# Revit family: Grohe_PlumbingFixtures_GrohthermSquare_ThermostaticMixer_24078000a
name_source: partatom
category: Plumbing Fixtures
revit_build: Autodesk Revit 2016 (Build: 20150714_1515(x64)
units: mm (PartAtom-declared; Revit-internal decimal feet)

## family parameters
Cut with Voids When Loaded = No
Host = Face
OmniClass Number = 23.65.00.00
OmniClass Title = Supply and Distribution of Liquids and Gases
Part Type = Normal
Room Calculation Point = No
Round Connector Dimension = Use Diameter
Shared = No

## types (1)
- 24078000
    ADACompliant = No
    Assembly Code = C1030
    AssetType = Fixed
    BIMObjectName = Grohe_PlumbingFixtures_GrohthermSquare_ThermostaticMixer_24078000
    CWFU = 4.5
    ClassificationName = Uniclass2015
    ClassificationValue = Pr_40_20_87_07
    ColdWaterConnectionDiameter = 10 mm  [stored 0.0328084 ft]
    Color = Silver
    Cost = 0 $
    Default Elevation = 0 mm  [stored 0 ft]
    Description = Grohtherm, Thermostatic Mixer for 1 outlet with shut off valve, set for final installation for GROHE Rapido SmartBox 35 600 000, GROHE TurboStat compact cartridge with wax thermoelement, GROHE StarLight chrome finish, GROHE QuickFix escutcheon with covered shaft sealing and covered fixing, Metal escutcheon, retroactively 6° adjustable 
GROHE SafeStop safety button at 38°C, GROHE SafeStop Plus optional temperature limiter at 43°C included built-in non return valves and dirt strainers, ceramic stop valve , 120°, Flow performance: outlet B or C = 27 l/min, without roughing-in-set
    DurationUnit = Years
    Ecojoy = No
    ExpectedLife = 0
    Features = Grohtherm, Thermostatic Mixer for 1 outlet with shut off valve, set for final installation for GROHE Rapido SmartBox 35 600 000, GROHE TurboStat compact cartridge with wax thermoelement, GROHE StarLight chrome finish, GROHE QuickFix escutcheon with covered shaft sealing and covered fixing, Metal escutcheon, retroactively 6° adjustable 
GROHE SafeStop safety button at 38°C, GROHE SafeStop Plus optional temperature limiter at 43°C included built-in non return valves and dirt strainers, ceramic stop valve , 120°, Flow performance: outlet B or C = 27 l/min, without roughing-in-set
    Finish = Chrome
    HWFU = 4.5
    HotWaterConnectionDiameter = 10 mm  [stored 0.0328084 ft]
    IfcExportAs = IfcPipeFitting
    IfcExportType = IfcPipeFittingType
    Keynote = N13
    LowEmittingMaterial = No
    Manufacturer = Grohe
    ManufacturerName = Grohe
    MasterformatNumber = 01 52 19
    MasterformatTitle = Sanitary Facilities
    Material = Chrome
    Model = Grohtherm square shower
    ModelNumber = 24078000
    ModelReference = Grohtherm square shower
    NBSDescription = Water supply fittings for baths
    NBSObjectName = Grohe - Water supply fittings for baths
    NBSReference = 45-35-70/315
    NominalDepth = 0 mm  [stored 0 ft]
    NominalHeight = 0 mm  [stored 0 ft]
    NominalLength = 0 mm  [stored 0 ft]
    ProductionYear = 2018
    Type Comments = 24078000
    TypeName = Grohtherm square shower
    URL = https://www.grohe.co.uk
    WarrantyDurationLabor = 0
    WarrantyDurationParts = 0
    WarrantyDurationUnit = Years
    _BSBibleVersion = 15
    _BimSpecGuid = 0
    _CurrentRevision = 1
    _DistributedBy = www.bimstore.co.uk

note: [stored X ft] marks values corroborated as IEEE doubles in the binary element streams (Revit-internal decimal feet)

## geometry (parser evidence)
native form markers: Blend x10, Sweep x3
no freeform markers — native parametric forms only
